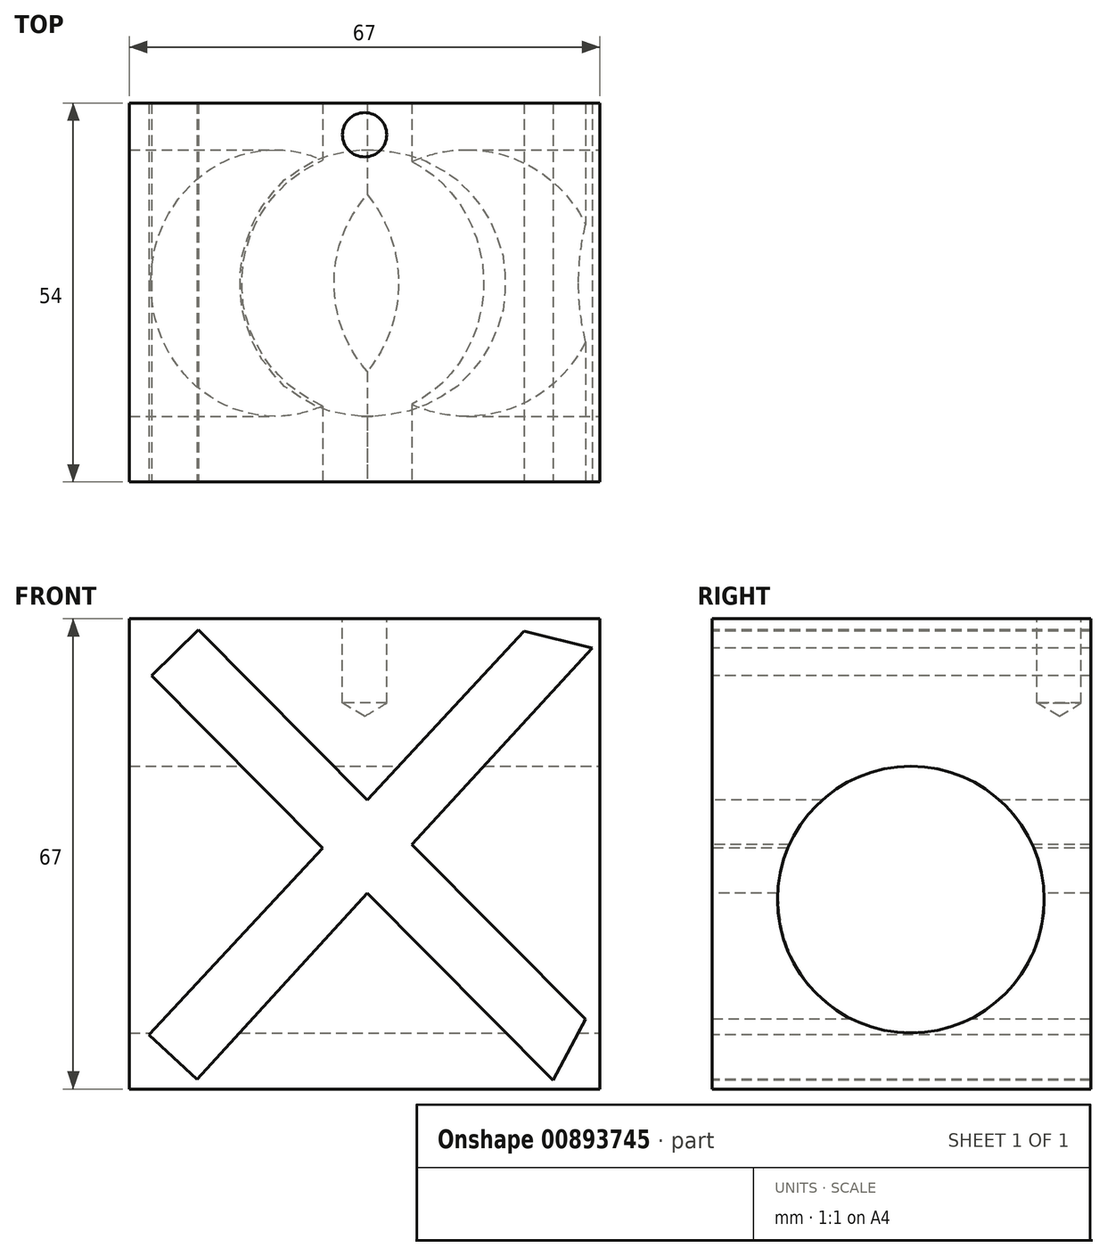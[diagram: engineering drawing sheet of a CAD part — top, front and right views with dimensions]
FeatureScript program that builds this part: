
annotation { "Feature Type Name" : "Feature", "Feature Type Description" : "" }
export const myFeature = defineFeature(function(context is Context, id is Id, definition is map)
    precondition{}
    {
        {
            var Q0;
            Q0=qCreatedBy(makeId("Front.planeOp"),FACE);
            var sketch = newSketch(context, id + "F0", { "sketchPlane" : qUnion([Q0])});
            skLineSegment(sketch, "E0.bottom", {"start": v(33.5, -33.5) * mm, "end": v(-33.5, -33.5) * mm});
            skLineSegment(sketch, "E0.top", {"start": v(33.5, 33.5) * mm, "end": v(-33.5, 33.5) * mm});
            skLineSegment(sketch, "E0.left", {"start": v(33.5, -33.5) * mm, "end": v(33.5, 33.5) * mm});
            skLineSegment(sketch, "E0.right", {"start": v(-33.5, -33.5) * mm, "end": v(-33.5, 33.5) * mm});
            skPoint(sketch, "E0.middle", {"position": v(0, 0) * mm});
            skLineSegment(sketch, "E1", {"start": v(-33.5, -28.73) * mm, "end": v(24.38, 33.5) * mm});
            skLineSegment(sketch, "E2", {"start": v(-25.17, -33.5) * mm, "end": v(33.5, 30.5) * mm});
            skLineSegment(sketch, "E3", {"start": v(-33.5, 28.57) * mm, "end": v(28.1, -33.5) * mm});
            skLineSegment(sketch, "E4", {"start": v(-25.26, 33.5) * mm, "end": v(33.5, -25.57) * mm});
            skLineSegment(sketch, "E5", {"start": v(22.74, 31.74) * mm, "end": v(32.47, 29.37) * mm});
            skLineSegment(sketch, "E6", {"start": v(-23.71, 31.94) * mm, "end": v(-30.33, 25.38) * mm});
            skLineSegment(sketch, "E7", {"start": v(-30.73, -25.75) * mm, "end": v(-23.9, -32.11) * mm});
            skLineSegment(sketch, "E8", {"start": v(31.48, -23.54) * mm, "end": v(26.83, -32.23) * mm});
            skSolve(sketch);
        }
        {
            var Q0;
            Q0=makeQuery(id+"F0.imprint","IMPRINT",FACE,{"disambiguationData":[TD([[makeQuery(id+"F0.imprint","IMPRINT",EDGE,{"derivedFrom":sQuery(id+"F0.wireOp",EDGE,"E0.bottom")}),-1.0]])]});
            var Q1;
            {var subQ0=sQuery(id+"F0.wireOp",EDGE,"ge1MqmDq-L9oZ-g4oQ-mAcj-TKKaD9TvBPy2");var subQ1=sQuery(id+"F0.wireOp",EDGE,"E0.right");var subQ2=makeQuery(id+"F0.imprint","INTERSECT",VERTEX,{"derivedFrom":[subQ1,subQ0]});Q1=makeQuery(id+"F0.imprint","IMPRINT",FACE,{"disambiguationData":[TD([[makeQuery(id+"F0.imprint","IMPRINT",EDGE,{"disambiguationData":[TD([[subQ2,-1.0]])],"derivedFrom":subQ1}),-1.0]])]});}
            var Q2;
            {var subQ0=sQuery(id+"F0.wireOp",EDGE,"ge1MqmDq-L9oZ-g4oQ-mAcj-TKKaD9TvBPy2");var subQ1=sQuery(id+"F0.wireOp",EDGE,"E0.top");var subQ2=makeQuery(id+"F0.imprint","INTERSECT",VERTEX,{"derivedFrom":[subQ1,subQ0]});Q2=makeQuery(id+"F0.imprint","IMPRINT",FACE,{"disambiguationData":[TD([[makeQuery(id+"F0.imprint","IMPRINT",EDGE,{"disambiguationData":[TD([[subQ2,-1.0]])],"derivedFrom":subQ1}),1.0]])]});}
            var Q3;
            {var subQ0=sQuery(id+"F0.wireOp",EDGE,"07cNTFpt-U9ia-FtVp-f2gg-7k5TWEXZu4MD");var subQ1=sQuery(id+"F0.wireOp",EDGE,"E0.left");var subQ2=makeQuery(id+"F0.imprint","INTERSECT",VERTEX,{"derivedFrom":[subQ1,subQ0]});Q3=makeQuery(id+"F0.imprint","IMPRINT",FACE,{"disambiguationData":[TD([[makeQuery(id+"F0.imprint","IMPRINT",EDGE,{"disambiguationData":[TD([[subQ2,1.0]])],"derivedFrom":subQ1}),1.0]])]});}
            extrude(context, id + "F1", {"entities" : qUnion([Q0, Q1, Q2, Q3]), "oppositeDirection" : true, "depth" : 54 * mm, "offsetDistance" : 25.4 * mm});
        }
        {
            var Q0;
            Q0=makeQuery(id+"F1.opExtrude","SWEPT_FACE",FACE,{"disambiguationData":[OSD([sQuery(id+"F0.wireOp",EDGE,"E0.left")])]});
            var sketch = newSketch(context, id + "F2", { "sketchPlane" : qUnion([Q0])});
            skLineSegment(sketch, "E9", {"start": v(45.05, 2.59) * mm, "end": v(54, 2.59) * mm});
            skLineSegment(sketch, "E10", {"start": v(44.57, -16.41) * mm, "end": v(54, -16.41) * mm});
            skArc(sketch, "E11", {"start": v(45.05, 2.59) * mm, "mid": v(9.37, -6.02) * mm, "end": v(44.57, -16.41) * mm});
            skLineSegment(sketch, "E12", {"start": v(54, 25.83) * mm, "end": v(25, 25.83) * mm});
            skLineSegment(sketch, "E13", {"start": v(54, 22.33) * mm, "end": v(24.84, 22.33) * mm});
            skLineSegment(sketch, "E14", {"start": v(24.84, 22.33) * mm, "end": v(25, 25.83) * mm});
            skSolve(sketch);
        }
        {
            var Q0;
            Q0=sQuery(id+"F2.wireOp",VERTEX,"E11.center");
            var Q1;
            Q1=makeQuery(id+"F1.opExtrude","SWEPT_BODY",BODY,{"disambiguationData":[OSD([sQuery(id+"F0.wireOp",EDGE,"E0.bottom"),sQuery(id+"F0.wireOp",EDGE,"E0.top"),sQuery(id+"F0.wireOp",EDGE,"E0.left"),sQuery(id+"F0.wireOp",EDGE,"E0.right"),sQuery(id+"F0.wireOp",EDGE,"E1"),sQuery(id+"F0.wireOp",EDGE,"E2"),sQuery(id+"F0.wireOp",EDGE,"E3"),sQuery(id+"F0.wireOp",EDGE,"E4"),sQuery(id+"F0.wireOp",EDGE,"E5"),sQuery(id+"F0.wireOp",EDGE,"E6"),sQuery(id+"F0.wireOp",EDGE,"E7"),sQuery(id+"F0.wireOp",EDGE,"E8")])]});
            hole(context, id + "F3", {"style" : HoleStyle.SIMPLE, "endStyle" : HoleEndStyle.THROUGH, "holeDiameter" : 38 * mm, "majorDiameter" : 5 * mm, "isTappedThrough" : true, "tappedDepth" : 12 * mm, "tapClearance" : 3, "locations" : qUnion([Q0]), "scope" : qUnion([Q1])});
        }
        {
            var Q0;
            Q0=makeQuery(id+"F1.opExtrude","SWEPT_FACE",FACE,{"disambiguationData":[OSD([sQuery(id+"F0.wireOp",EDGE,"E0.top")])]});
            var sketch = newSketch(context, id + "F4", { "sketchPlane" : qUnion([Q0])});
            skCircle(sketch, "E15", {"center": v(0, 49.49) * mm, "radius": 3.15 * mm});
            skPoint(sketch, "E16", {"position": v(0, 54) * mm});
            skSolve(sketch);
        }
        {
            var Q0;
            Q0=sQuery(id+"F4.wireOp",VERTEX,"E15.center");
            var Q1;
            Q1=makeQuery(id+"F1.opExtrude","SWEPT_BODY",BODY,{"disambiguationData":[OSD([sQuery(id+"F0.wireOp",EDGE,"E0.bottom"),sQuery(id+"F0.wireOp",EDGE,"E0.top"),sQuery(id+"F0.wireOp",EDGE,"E0.left"),sQuery(id+"F0.wireOp",EDGE,"E0.right"),sQuery(id+"F0.wireOp",EDGE,"E1"),sQuery(id+"F0.wireOp",EDGE,"E2"),sQuery(id+"F0.wireOp",EDGE,"E3"),sQuery(id+"F0.wireOp",EDGE,"E4"),sQuery(id+"F0.wireOp",EDGE,"E5"),sQuery(id+"F0.wireOp",EDGE,"E6"),sQuery(id+"F0.wireOp",EDGE,"E7"),sQuery(id+"F0.wireOp",EDGE,"E8")])]});
            hole(context, id + "F5", {"style" : HoleStyle.SIMPLE, "endStyle" : HoleEndStyle.BLIND, "holeDiameter" : 6.3 * mm, "majorDiameter" : 5 * mm, "holeDepth" : 12 * mm, "isTappedThrough" : true, "tappedDepth" : 12 * mm, "tapClearance" : 3, "locations" : qUnion([Q0]), "scope" : qUnion([Q1])});
        }
    });
